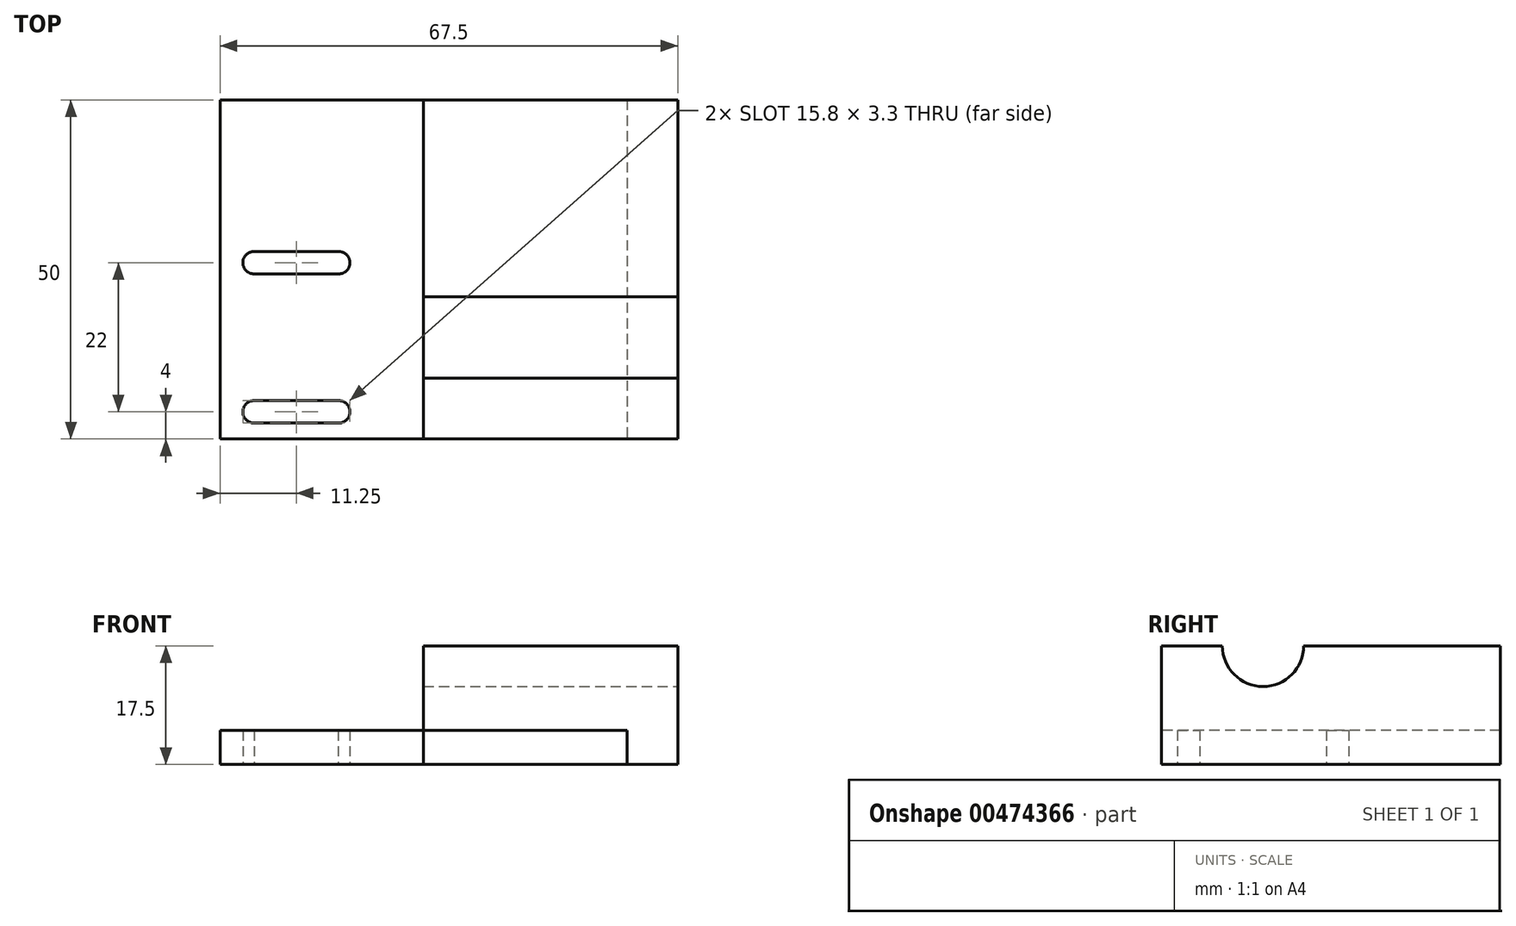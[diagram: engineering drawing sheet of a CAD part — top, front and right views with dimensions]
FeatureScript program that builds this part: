
annotation { "Feature Type Name" : "Feature", "Feature Type Description" : "" }
export const myFeature = defineFeature(function(context is Context, id is Id, definition is map)
    precondition{}
    {
        {
            var Q0;
            Q0=qCreatedBy(makeId("Top.planeOp"),FACE);
            var sketch = newSketch(context, id + "F0", { "sketchPlane" : qUnion([Q0])});
            skPoint(sketch, "E0.middle", {"position": v(0, 0) * mm});
            skLineSegment(sketch, "E1", {"start": v(0, 0) * mm, "end": v(-12.5, 0) * mm, "construction": true});
            skLineSegment(sketch, "E2", {"start": v(-12.5, -25) * mm, "end": v(-12.5, -10) * mm, "construction": true});
            skLineSegment(sketch, "E3", {"start": v(-12.5, -10) * mm, "end": v(-12.5, 1) * mm, "construction": true});
            skArc(sketch, "E4", {"start": v(-12.56, -0.65) * mm, "mid": v(-12.5, -0.65) * mm, "end": v(-12.44, -0.65) * mm});
            skLineSegment(sketch, "E5", {"start": v(-12.5, -10) * mm, "end": v(-25, -10) * mm, "construction": true});
            skLineSegment(sketch, "E6.bottom", {"start": v(30, 25) * mm, "end": v(-30, 25) * mm});
            skLineSegment(sketch, "E6.top", {"start": v(30, -25) * mm, "end": v(-30, -25) * mm});
            skLineSegment(sketch, "E6.left", {"start": v(30, 25) * mm, "end": v(30, -25) * mm});
            skLineSegment(sketch, "E6.right", {"start": v(-30, 25) * mm, "end": v(-30, -25) * mm});
            skLineSegment(sketch, "E7", {"start": v(-12.56, 2.65) * mm, "end": v(-12.44, 2.65) * mm});
            skLineSegment(sketch, "E8", {"start": v(-12.56, 2.65) * mm, "end": v(-24.94, 2.65) * mm});
            skLineSegment(sketch, "E9", {"start": v(-12.5, 1) * mm, "end": v(-7.5, 1) * mm, "construction": true});
            skLineSegment(sketch, "E10.MirrorCS", {"start": v(-12.56, -0.65) * mm, "end": v(-12.44, -0.65) * mm});
            skLineSegment(sketch, "E11.MirrorCS", {"start": v(-12.56, -0.65) * mm, "end": v(-25.06, -0.65) * mm});
            skArc(sketch, "E12.trimOffspring", {"start": v(-12.44, 2.65) * mm, "mid": v(-12.5, 2.65) * mm, "end": v(-12.56, 2.65) * mm});
            skLineSegment(sketch, "E13.trimOffspring", {"start": v(-17.56, 2.65) * mm, "end": v(-17.56, 2.65) * mm});
            skArc(sketch, "E14", {"start": v(-12.56, -0.65) * mm, "mid": v(-10.85, 1) * mm, "end": v(-12.56, 2.65) * mm});
            skLineSegment(sketch, "E15", {"start": v(-12.5, 1) * mm, "end": v(-25, 1) * mm, "construction": true});
            skArc(sketch, "E16", {"start": v(-24.94, 2.65) * mm, "mid": v(-26.65, 1) * mm, "end": v(-24.94, -0.65) * mm});
            skLineSegment(sketch, "E17.MirrorCS", {"start": v(-12.56, -19.35) * mm, "end": v(-22.56, -19.35) * mm});
            skArc(sketch, "E18.MirrorCS", {"start": v(-24.94, -22.65) * mm, "mid": v(-26.65, -21) * mm, "end": v(-24.94, -19.35) * mm});
            skLineSegment(sketch, "E19.MirrorCS", {"start": v(-12.56, -22.65) * mm, "end": v(-22.56, -22.65) * mm});
            skArc(sketch, "E20.MirrorCS", {"start": v(-12.56, -19.35) * mm, "mid": v(-10.85, -21) * mm, "end": v(-12.56, -22.65) * mm});
            skPoint(sketch, "E21.orphan", {"position": v(-22.56, 2.65) * mm});
            skPoint(sketch, "E22.orphan", {"position": v(-22.56, -0.65) * mm});
            skLineSegment(sketch, "E23.MirrorCS", {"start": v(-12.56, -19.35) * mm, "end": v(-25.06, -19.35) * mm});
            skLineSegment(sketch, "E24.MirrorCS", {"start": v(-12.56, -22.65) * mm, "end": v(-24.94, -22.65) * mm});
            skSolve(sketch);
        }
        {
            var Q0;
            Q0 = qSketchRegion(id + "F0", true);
            extrude(context, id + "F1", {"entities" : qUnion([Q0]), "depth" : 5 * mm});
        }
        {
            var Q0;
            Q0=qCreatedBy(makeId("Top.planeOp"),FACE);
            var sketch = newSketch(context, id + "F2", { "sketchPlane" : qUnion([Q0])});
            skLineSegment(sketch, "E25.bottom", {"start": v(37.5, 25) * mm, "end": v(-37.5, 25) * mm, "construction": true});
            skLineSegment(sketch, "E25.top", {"start": v(37.5, -25) * mm, "end": v(-37.5, -25) * mm, "construction": true});
            skLineSegment(sketch, "E25.left", {"start": v(37.5, 25) * mm, "end": v(37.5, -25) * mm, "construction": true});
            skLineSegment(sketch, "E25.right", {"start": v(-37.5, 25) * mm, "end": v(-37.5, -25) * mm, "construction": true});
            skPoint(sketch, "E25.middle", {"position": v(0, 0) * mm});
            skLineSegment(sketch, "E26", {"start": v(37.5, -25) * mm, "end": v(0, -25) * mm});
            skLineSegment(sketch, "E27", {"start": v(0, -25) * mm, "end": v(37.5, -25) * mm});
            skLineSegment(sketch, "E28", {"start": v(0, -25) * mm, "end": v(0, 25) * mm});
            skLineSegment(sketch, "E29", {"start": v(0, 25) * mm, "end": v(37.5, 25) * mm});
            skLineSegment(sketch, "E30", {"start": v(37.5, -25) * mm, "end": v(37.5, 25) * mm});
            skSolve(sketch);
        }
        {
            var Q0;
            Q0 = qSketchRegion(id + "F2", true);
            extrude(context, id + "F3", {"entities" : qUnion([Q0]), "depth" : 30 * mm});
        }
        {
            var Q0;
            Q0=makeQuery(id+"F3.opExtrude","SWEPT_FACE",FACE,{"disambiguationData":[OSD([sQuery(id+"F2.wireOp",EDGE,"E30")])]});
            var sketch = newSketch(context, id + "F4", { "sketchPlane" : qUnion([Q0])});
            skPoint(sketch, "E31.middle", {"position": v(0, 0) * mm});
            skCircle(sketch, "E32", {"center": v(-10, 17.5) * mm, "radius": 6 * mm});
            skLineSegment(sketch, "E33", {"start": v(-10, 17.5) * mm, "end": v(-25, 17.5) * mm, "construction": true});
            skLineSegment(sketch, "E34", {"start": v(-10, 17.5) * mm, "end": v(-10, 0) * mm, "construction": true});
            skSolve(sketch);
        }
        {
            var Q0;
            Q0 = qSketchRegion(id + "F4", true);
            var Q1;
            Q1=makeQuery(id+"F3.opExtrude","SWEPT_FACE",FACE,{"disambiguationData":[OSD([sQuery(id+"F2.wireOp",EDGE,"E28")])]});
            extrude(context, id + "F5", {"entities" : qUnion([Q0]), "operationType" : NewBodyOperationType.REMOVE, "endBound" : BoundingType.UP_TO_SURFACE, "oppositeDirection" : true, "endBoundEntityFace" : qUnion([Q1]), "depth" : 25 * mm});
        }
        {
            var Q0;
            Q0=makeQuery(id+"F3.opExtrude","CAP_FACE",FACE,{"disambiguationData":[OSD([sQuery(id+"F2.wireOp",EDGE,"E27"),sQuery(id+"F2.wireOp",EDGE,"E28"),sQuery(id+"F2.wireOp",EDGE,"E29"),sQuery(id+"F2.wireOp",EDGE,"E30")])],"isStart":false});
            var sketch = newSketch(context, id + "F6", { "sketchPlane" : qUnion([Q0])});
            skLineSegment(sketch, "E35.bottom", {"start": v(0, 25) * mm, "end": v(37.5, 25) * mm});
            skLineSegment(sketch, "E35.top", {"start": v(0, -25) * mm, "end": v(37.5, -25) * mm});
            skLineSegment(sketch, "E35.left", {"start": v(0, 25) * mm, "end": v(0, -25) * mm});
            skLineSegment(sketch, "E35.right", {"start": v(37.5, 25) * mm, "end": v(37.5, -25) * mm});
            skSolve(sketch);
        }
        {
            var Q0;
            Q0 = qSketchRegion(id + "F6", true);
            extrude(context, id + "F7", {"entities" : qUnion([Q0]), "operationType" : NewBodyOperationType.REMOVE, "oppositeDirection" : true, "depth" : 12.5 * mm});
        }
    });
